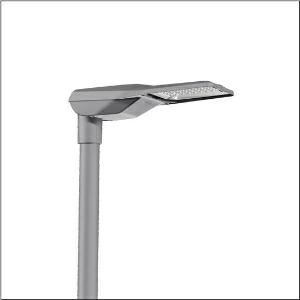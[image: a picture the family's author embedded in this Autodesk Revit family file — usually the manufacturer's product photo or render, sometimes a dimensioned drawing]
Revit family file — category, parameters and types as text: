
# Revit family: streetlight_sl_21_iq_mini___stw1_0a_5xe2e61d08hb_c7c8
name_source: partatom
category: Lighting Fixtures
units: mm (PartAtom-declared; Revit-internal decimal feet)

## family parameters
Cut with Voids When Loaded = No
Host = Face
Light Source = No
Part Type = Normal
Room Calculation Point = No
Round Connector Dimension = Use Diameter
Shared = No

## types (1)
- --- (1 x LED, 8480 lm, 70.9 W, 2700K)
    Apparent Load = 71 VA
    CIE Flux Codes = 38 75 98 100 100
    Color Rendering = 70
    Color Temperature = 2700K
    Default Elevation = 1800 mm
    Description = Streetlight SL 21 iQ mini, mast luminaire, primary light control with lens, of PMMA, primary optical cover: cover, of toughened safety glass, transparent, light distribution: STW1.0a, light emission: direct distribution, primary light characteristic: asymmetric, installation type: post-top, side-entry, LED, High Power LED, rated luminous flux: 8.480lm, luminous efficacy: 120lm/W, light colour: 727, colour temperature: 2700K, control: Auto-Match, Temp-Guard, Lumen-Switch, Night-Set, Smart-Wire, Light-Fading, Desk-Remote (wireless, voltage-free reading and setting of iQ features in the workshop via application-optimized NFC function/RFID function), optimised constant luminous flux control (CLO 2.0), pre-setting: linear dimming characteristic, mains connection: 220..240V, AC, 50/60Hz, start of lifetime: 71W, end of service life: 75W, reduction: 31W, luminaire housing, of diecast aluminium, powder-coated, Siteco® metallic grey (DB 702S), corrosivity category C5 mid according to DIN EN ISO 12944, please order mast flange separately, inclination adjustable: 0°, 5°, 10°, 15°, sealing non-destructively replaceable, multi-level sealing system, length: 628mm, width: 235mm, height: 110mm, mast flange for spigot size: 42mm (side-entry): 5XC10008XM4, 60/48mm (side-entry/post-top): 5XC10108XM2, 76/60mm (side-entry/post-top): 5XC10108XM1, protection rating (complete): IP66, insulation class (complete): insulation class II (safety insulation), certification: CE, ENEC, ENEC+, VDE, impact resistance: IK09, permissible operating ambient temperature for outdoor applications: -40..+50°C, standard-compliant lighting for roads and squares, packaging unit: 1 piece

Light Distribution: STW1.0a
    Height = 110 mm
    Lamp = 1 x LED
    Lamp Light Flux = 8480 lm
    Lamp Power = 70.9 W
    Lamp count = 1
    Length = 625 mm
    Luminous efficacy = 120 lm/W
    Manufacturer = Siteco
    ModVariant = No
    Model = 5XE2E61D08HB
    Number of Poles = 1
    OnlyDefault = Yes
    Power Factor = 1
    Product Name = Streetlight SL 21 iQ mini | STW1.0a
    Product group = mast luminaire | pylon top
    ProductGroupID = 6100
    Protection Class = Protection class II
    Protection Degree = IP 66
    RLX_Detail_Level = 1
    RLX_Emergency_Light_Flux = 0 lm
    RLX_Emergency_Type = 0
    RLX_Emergency_Type_DB = No
    RlxData = <blob elided: 92289 chars, md5=1f92839d>
    Socket = socket
    Standby Power = 0 W
    System Light Flux = 8480 lm
    System Power = 71 W
    Type Comments = factory setting: luminous flux: 100 % | dim-lin: 254 | 711 mA
    Type Image = l_1003519.jpg
    URL = http://relux.com
    VarID = @adj_128293
    Voltage = 0 V
    Weight = 0.00 kg
    Width = 234 mm

## geometry (parser evidence)
native form markers: Blend x4, Sweep x10
no freeform markers — native parametric forms only
